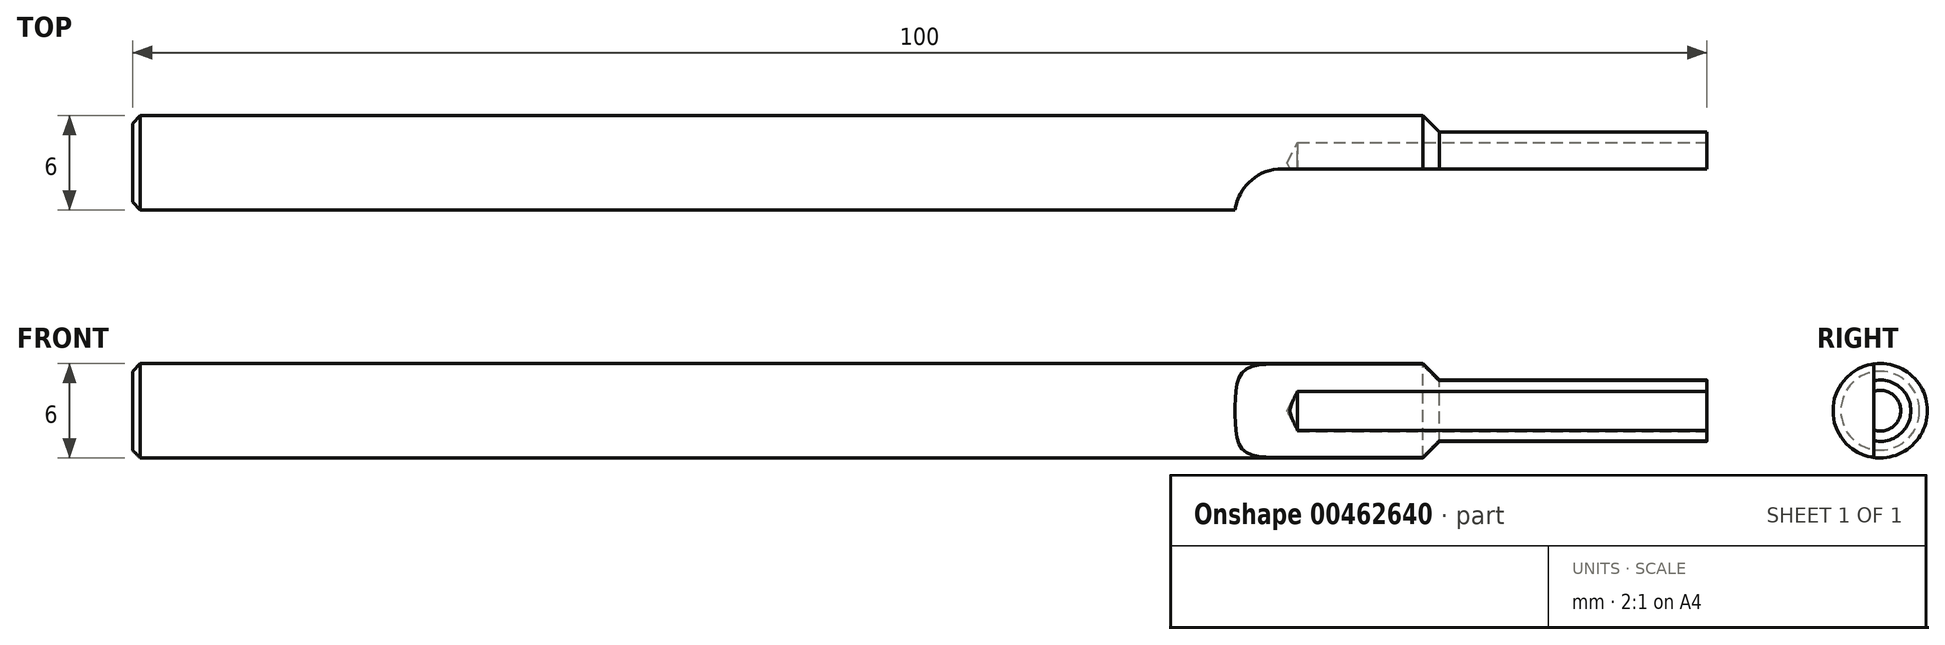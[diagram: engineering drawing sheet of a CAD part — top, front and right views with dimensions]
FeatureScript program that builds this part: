
annotation { "Feature Type Name" : "Feature", "Feature Type Description" : "" }
export const myFeature = defineFeature(function(context is Context, id is Id, definition is map)
    precondition{}
    {
        {
            var Q0;
            Q0=qCreatedBy(makeId("Front.planeOp"),FACE);
            var sketch = newSketch(context, id + "F0", { "sketchPlane" : qUnion([Q0])});
            skLineSegment(sketch, "E0", {"start": v(-81.95, 0) * mm, "end": v(-81.95, 3) * mm});
            skLineSegment(sketch, "E1", {"start": v(-81.95, 3) * mm, "end": v(0, 3) * mm});
            skLineSegment(sketch, "E2", {"start": v(0, 3) * mm, "end": v(1.05, 1.95) * mm});
            skLineSegment(sketch, "E3", {"start": v(1.05, 1.95) * mm, "end": v(18.05, 1.95) * mm});
            skLineSegment(sketch, "E4", {"start": v(18.05, 1.95) * mm, "end": v(18.05, 0) * mm});
            skLineSegment(sketch, "E5", {"start": v(18.05, 0) * mm, "end": v(-81.95, 0) * mm});
            skLineSegment(sketch, "E6.MirrorCS", {"start": v(18.05, -1.95) * mm, "end": v(18.05, 0) * mm});
            skLineSegment(sketch, "E7.MirrorCS", {"start": v(0, -3) * mm, "end": v(1.05, -1.95) * mm});
            skLineSegment(sketch, "E8.MirrorCS", {"start": v(-81.95, -3) * mm, "end": v(0, -3) * mm});
            skLineSegment(sketch, "E9.MirrorCS", {"start": v(-81.95, 0) * mm, "end": v(-81.95, -3) * mm});
            skLineSegment(sketch, "E10.MirrorCS", {"start": v(1.05, -1.95) * mm, "end": v(18.05, -1.95) * mm});
            skLineSegment(sketch, "E11", {"start": v(18.05, 1.3) * mm, "end": v(-7.95, 1.3) * mm});
            skLineSegment(sketch, "E12", {"start": v(-7.95, 1.3) * mm, "end": v(-8.64, 0) * mm});
            skLineSegment(sketch, "E13", {"start": v(-8.64, 0) * mm, "end": v(18.05, 0) * mm});
            skSolve(sketch);
        }
        {
            var Q0;
            Q0=makeQuery(id+"F0.imprint","IMPRINT",FACE,{"disambiguationData":[TD([[makeQuery(id+"F0.imprint","IMPRINT",EDGE,{"derivedFrom":sQuery(id+"F0.wireOp",EDGE,"E0")}),-1.0]])]});
            var Q1;
            Q1=sQuery(id+"F0.wireOp",EDGE,"E5");
            revolve(context, id + "F1", {"entities" : qUnion([Q0]), "axis" : qUnion([Q1]), "revolveType" : RevolveType.FULL});
        }
        {
            var Q0;
            Q0=qCreatedBy(makeId("Top.planeOp"),FACE);
            cPlane(context, id + "F2", {"entities" : qUnion([Q0]), "cplaneType" : CPlaneType.OFFSET, "offset" : 3 * mm, "width" : 150 * mm, "height" : 150 * mm});
        }
        {
            var Q0;
            Q0=qCreatedBy(id+"F2.planeOp",FACE);
            var sketch = newSketch(context, id + "F3", { "sketchPlane" : qUnion([Q0])});
            skCircle(sketch, "E14", {"center": v(-8.95, -3.4) * mm, "radius": 3 * mm});
            skLineSegment(sketch, "E15", {"start": v(-8.95, -3.4) * mm, "end": v(-8.95, -0.4) * mm});
            skLineSegment(sketch, "E16", {"start": v(-8.95, -0.4) * mm, "end": v(18.05, -0.4) * mm});
            skLineSegment(sketch, "E17", {"start": v(-8.95, -3.4) * mm, "end": v(18.05, -3.4) * mm});
            skLineSegment(sketch, "E18.0", {"start": v(18.05, 1.95) * mm, "end": v(18.05, -1.95) * mm});
            skLineSegment(sketch, "E19", {"start": v(18.05, -0.4) * mm, "end": v(18.05, -3.4) * mm});
            skSolve(sketch);
        }
        {
            var Q0;
            {var subQ0=sQuery(id+"F3.wireOp",EDGE,"E15");Q0=makeQuery(id+"F3.imprint","IMPRINT",FACE,{"disambiguationData":[TD([[makeQuery(id+"F3.imprint","IMPRINT",EDGE,{"derivedFrom":subQ0}),1.0]])]});}
            var Q1;
            {var subQ0=sQuery(id+"F3.wireOp",EDGE,"E16");Q1=makeQuery(id+"F3.imprint","IMPRINT",FACE,{"disambiguationData":[TD([[makeQuery(id+"F3.imprint","IMPRINT",EDGE,{"derivedFrom":subQ0}),-1.0]])]});}
            var Q2;
            {var subQ0=sQuery(id+"F3.wireOp",EDGE,"E15");Q2=makeQuery(id+"F3.imprint","IMPRINT",FACE,{"disambiguationData":[TD([[makeQuery(id+"F3.imprint","IMPRINT",EDGE,{"derivedFrom":subQ0}),-1.0]])]});}
            extrude(context, id + "F4", {"entities" : qUnion([Q0, Q1, Q2]), "operationType" : NewBodyOperationType.REMOVE, "oppositeDirection" : true, "depth" : 25 * mm});
        }
        {
            var Q0;
            Q0=makeQuery(id+"F1.opRevolve","SWEPT_EDGE",EDGE,{"disambiguationData":[OSD([sQuery(id+"F0.wireOp",EDGE,"E0"),sQuery(id+"F0.wireOp",EDGE,"E1")])]});
            chamfer(context, id + "F5", {"entities" : qUnion([Q0]), "width" : 0.5 * mm, "tangentPropagation" : true});
        }
    });
